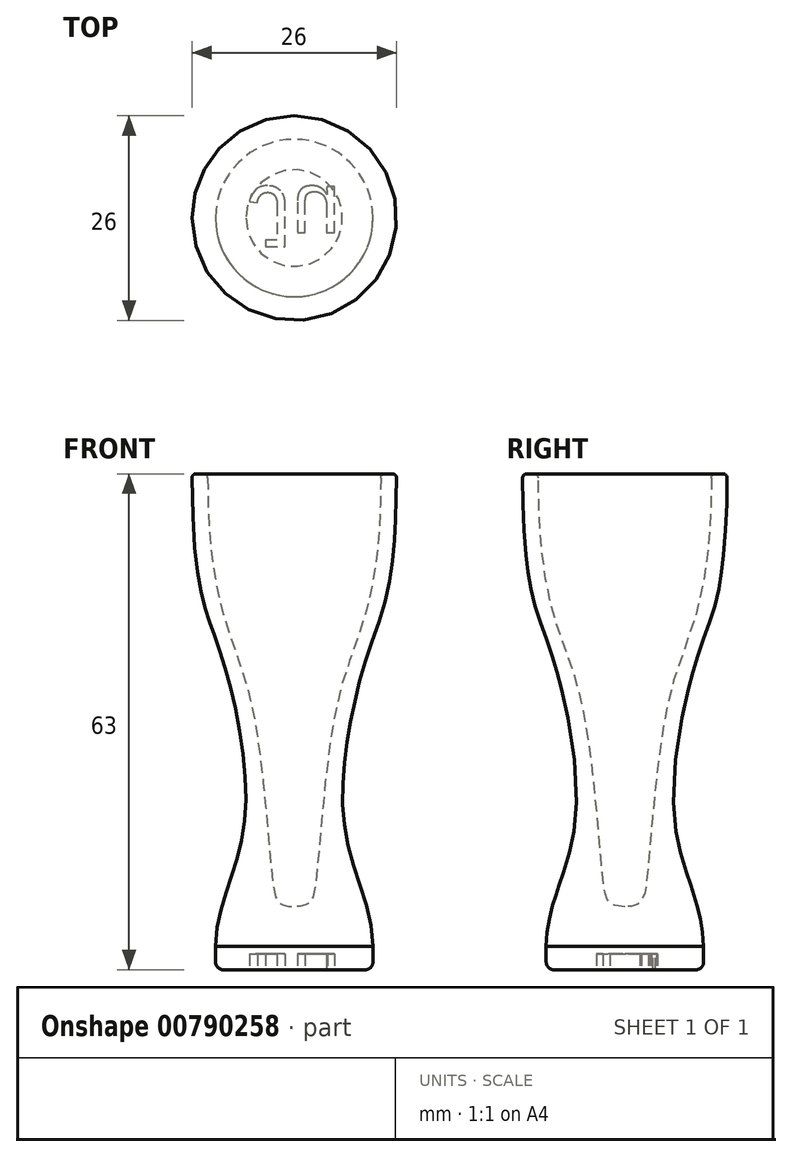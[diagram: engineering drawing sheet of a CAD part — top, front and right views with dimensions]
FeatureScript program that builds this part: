
annotation { "Feature Type Name" : "Feature", "Feature Type Description" : "" }
export const myFeature = defineFeature(function(context is Context, id is Id, definition is map)
    precondition{}
    {
        {
            var Q0;
            Q0=qCreatedBy(makeId("Right.planeOp"),FACE);
            var sketch = newSketch(context, id + "F0", { "sketchPlane" : qUnion([Q0])});
            skLineSegment(sketch, "E0", {"start": v(-13, 60) * mm, "end": v(-11, 60) * mm});
            skPoint(sketch, "E1", {"position": v(0, 5) * mm});
            skPoint(sketch, "E2", {"position": v(-6.34, 15.51) * mm});
            skPoint(sketch, "E3", {"position": v(-2.73, 7.98) * mm});
            skPoint(sketch, "E4", {"position": v(-9.39, 37.3) * mm});
            skPoint(sketch, "E5", {"position": v(-2.16, 5.84) * mm});
            skFitSpline(sketch, "E6", {"points": [v(-10, 0) * mm, v(-6.34, 15.51) * mm, v(-9.39, 37.3) * mm, v(-13, 60) * mm], "startDerivative": vector(1.14, 56.54) * mm, "endDerivative": vector(-1.1, 129.67) * mm});
            skPoint(sketch, "E7", {"position": v(-5.65, 31.7) * mm});
            skFitSpline(sketch, "E8", {"points": [v(0, 5) * mm, v(-2.16, 5.84) * mm, v(-2.73, 7.98) * mm, v(-5.65, 31.7) * mm, v(-11, 60) * mm], "startDerivative": vector(-38.49, 0.42) * mm, "endDerivative": vector(-0.05, 131.64) * mm});
            skLineSegment(sketch, "E9", {"start": v(-10, 0) * mm, "end": v(-10, -3) * mm});
            skLineSegment(sketch, "E10", {"start": v(-10, -3) * mm, "end": v(0, -3) * mm});
            skLineSegment(sketch, "E11", {"start": v(0, 5) * mm, "end": v(0, -3) * mm});
            skSolve(sketch);
        }
        {
            var Q0;
            Q0=qCreatedBy(makeId("Right.planeOp"),FACE);
            var sketch = newSketch(context, id + "F1", { "sketchPlane" : qUnion([Q0])});
            skLineSegment(sketch, "E12", {"start": v(0, 0) * mm, "end": v(0, 61.02) * mm});
            skSolve(sketch);
        }
        {
            var Q0;
            Q0=makeQuery(id+"F0.imprint","IMPRINT",FACE,{"disambiguationData":[TD([[makeQuery(id+"F0.imprint","IMPRINT",EDGE,{"derivedFrom":sQuery(id+"F0.wireOp",EDGE,"E0")}),-1.0]])]});
            var Q1;
            Q1=sQuery(id+"F1.wireOp",EDGE,"E12");
            revolve(context, id + "F2", {"surfaceOperationType" : NewSurfaceOperationType.NEW, "entities" : qUnion([Q0]), "axis" : qUnion([Q1]), "revolveType" : RevolveType.FULL});
        }
        {
            var Q0;
            Q0=makeQuery(id+"F2.opRevolve","SWEPT_EDGE",EDGE,{"disambiguationData":[OSD([sQuery(id+"F0.wireOp",EDGE,"E0"),sQuery(id+"F0.wireOp",EDGE,"E8")])]});
            var Q1;
            Q1=makeQuery(id+"F2.opRevolve","SWEPT_EDGE",EDGE,{"disambiguationData":[OSD([sQuery(id+"F0.wireOp",EDGE,"E0"),sQuery(id+"F0.wireOp",EDGE,"E6")])]});
            fillet(context, id + "F3", {"entities" : qUnion([Q0, Q1]), "radius" : 0.5 * mm, "tangentPropagation" : true, "allowEdgeOverflow" : false});
        }
        {
            var Q0;
            Q0=makeQuery(id+"F2.opRevolve","SWEPT_EDGE",EDGE,{"disambiguationData":[OSD([sQuery(id+"F0.wireOp",EDGE,"E9"),sQuery(id+"F0.wireOp",EDGE,"E10")])]});
            fillet(context, id + "F4", {"entities" : qUnion([Q0]), "radius" : 1 * mm, "tangentPropagation" : true, "allowEdgeOverflow" : false});
        }
        {
            var Q0;
            Q0=makeQuery(id+"F2.opRevolve","SWEPT_FACE",FACE,{"disambiguationData":[OSD([sQuery(id+"F0.wireOp",EDGE,"E10")])]});
            var sketch = newSketch(context, id + "F5", { "sketchPlane" : qUnion([Q0])});
            skText(sketch, "E13", { "text": "Ju", "fontName": "Arimo-Regular.ttf"});
            const initialGuessF5  = {"E13": [-0.00588, -0.004, 1, 0, 0.008]};
            skSetInitialGuess(sketch, initialGuessF5);
            skSolve(sketch);
        }
        {
            var Q0;
            Q0 = qSketchRegion(id + "F5", true);
            extrude(context, id + "F6", {"entities" : qUnion([Q0]), "operationType" : NewBodyOperationType.REMOVE, "oppositeDirection" : true, "depth" : 2 * mm, "offsetDistance" : 25 * mm});
        }
    });
